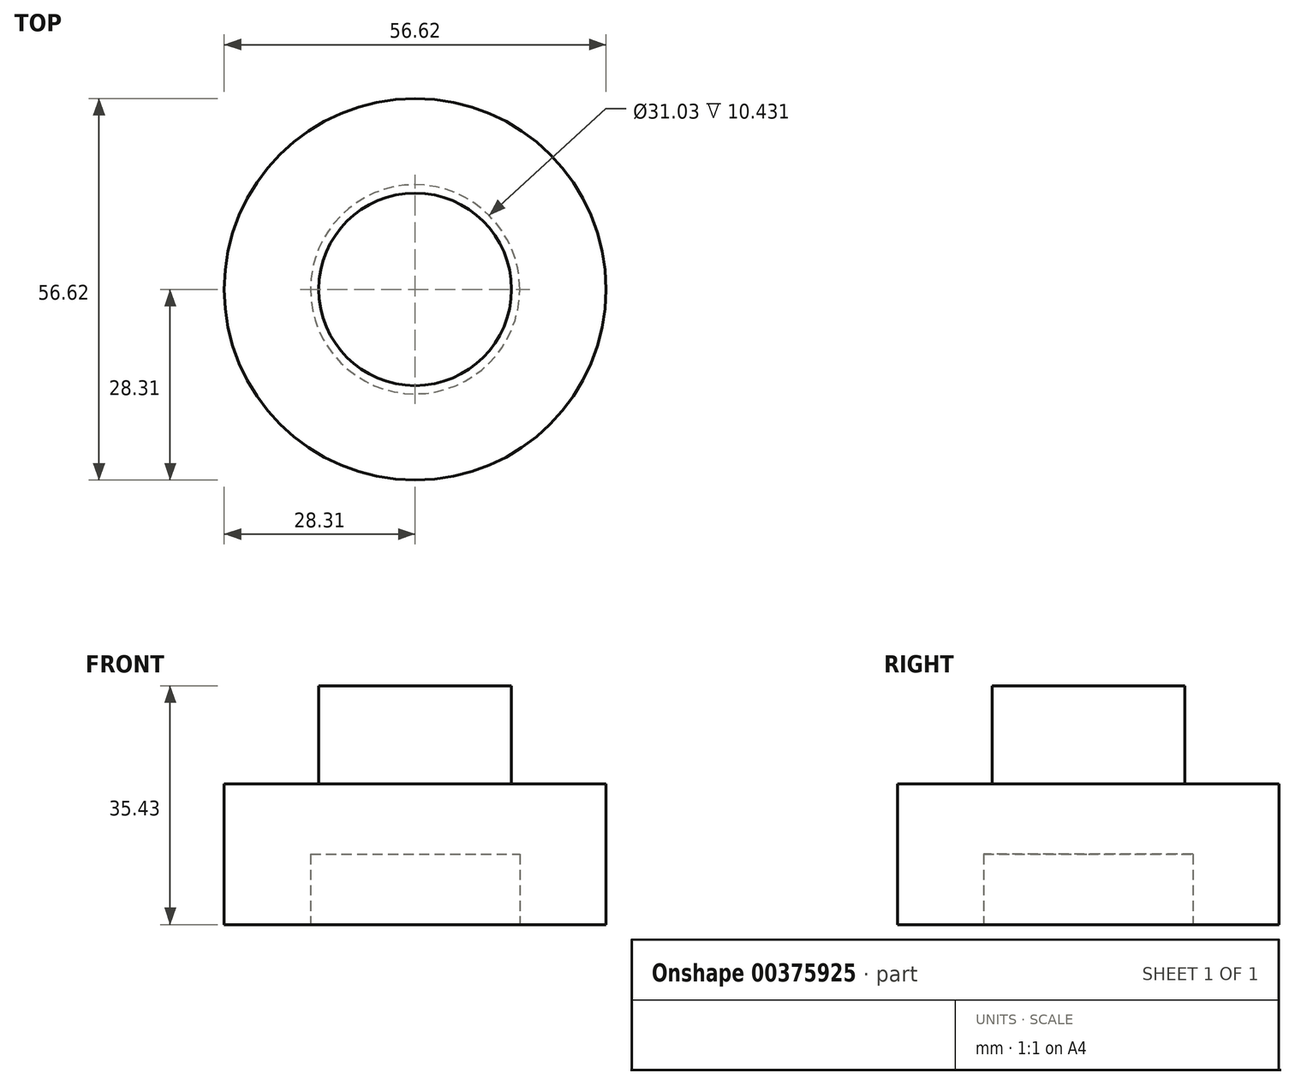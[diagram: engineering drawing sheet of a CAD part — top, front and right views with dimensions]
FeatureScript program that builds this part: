
annotation { "Feature Type Name" : "Feature", "Feature Type Description" : "" }
export const myFeature = defineFeature(function(context is Context, id is Id, definition is map)
    precondition{}
    {
        {
            var Q0;
            Q0=qCreatedBy(makeId("Right.planeOp"),FACE);
            var sketch = newSketch(context, id + "F0", { "sketchPlane" : qUnion([Q0])});
            skLineSegment(sketch, "E0", {"start": v(0, 0) * mm, "end": v(0, 25) * mm});
            skLineSegment(sketch, "E1", {"start": v(0, 25) * mm, "end": v(14.29, 25) * mm});
            skLineSegment(sketch, "E2", {"start": v(14.29, 25) * mm, "end": v(14.29, 10.44) * mm});
            skLineSegment(sketch, "E3", {"start": v(14.29, 10.44) * mm, "end": v(28.3, 10.44) * mm});
            skLineSegment(sketch, "E4", {"start": v(28.3, 10.44) * mm, "end": v(28.3, -10.43) * mm});
            skLineSegment(sketch, "E5", {"start": v(28.3, -10.43) * mm, "end": v(15.51, -10.43) * mm});
            skLineSegment(sketch, "E6", {"start": v(15.51, -10.43) * mm, "end": v(15.51, 0) * mm});
            skLineSegment(sketch, "E7", {"start": v(15.51, 0) * mm, "end": v(0, 0) * mm});
            skSolve(sketch);
        }
        {
            var Q0;
            Q0=makeQuery(id+"F0.imprint","IMPRINT",FACE,{"disambiguationData":[TD([[makeQuery(id+"F0.imprint","IMPRINT",EDGE,{"derivedFrom":sQuery(id+"F0.wireOp",EDGE,"E0")}),-1.0]])]});
            var Q1;
            Q1=sQuery(id+"F0.wireOp",EDGE,"E0");
            revolve(context, id + "F1", {"entities" : qUnion([Q0]), "axis" : qUnion([Q1]), "revolveType" : RevolveType.FULL});
        }
    });
